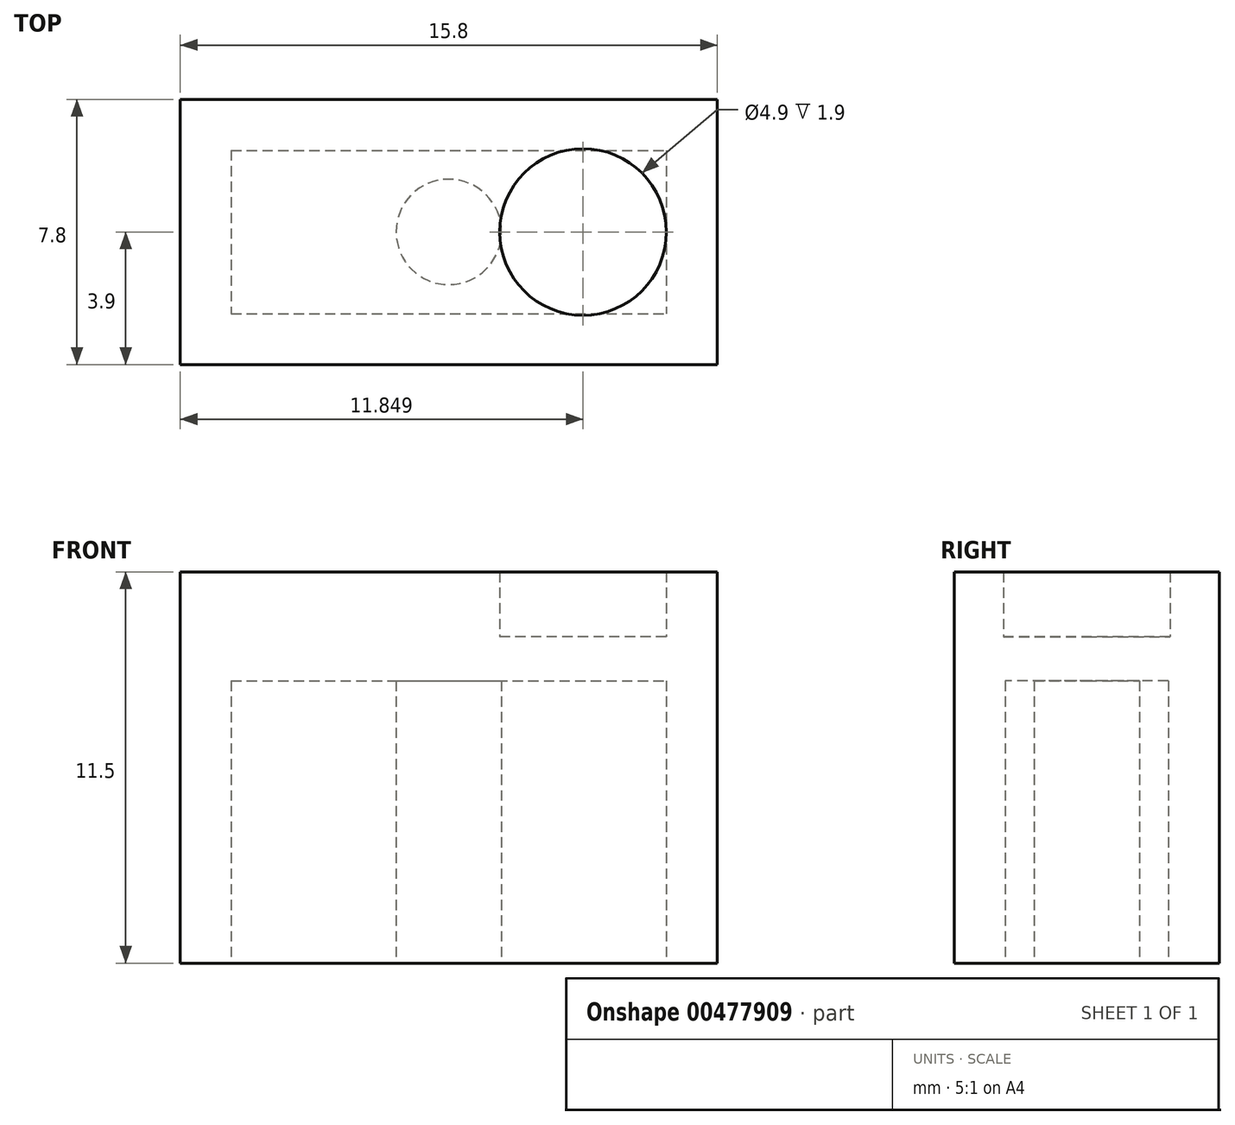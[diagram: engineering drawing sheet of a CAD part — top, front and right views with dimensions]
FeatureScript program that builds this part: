
annotation { "Feature Type Name" : "Feature", "Feature Type Description" : "" }
export const myFeature = defineFeature(function(context is Context, id is Id, definition is map)
    precondition{}
    {
        {
            var Q0;
            Q0=qCreatedBy(makeId("Front.planeOp"),FACE);
            var sketch = newSketch(context, id + "F0", { "sketchPlane" : qUnion([Q0])});
            skLineSegment(sketch, "E0", {"start": v(-64.18, -22.45) * mm, "end": v(-48.38, -22.45) * mm});
            skLineSegment(sketch, "E1", {"start": v(-48.38, -22.45) * mm, "end": v(-48.38, -12.85) * mm});
            skLineSegment(sketch, "E2", {"start": v(-48.38, -12.85) * mm, "end": v(-64.18, -12.85) * mm});
            skLineSegment(sketch, "E3", {"start": v(-64.18, -12.85) * mm, "end": v(-64.18, -22.45) * mm});
            skSolve(sketch);
        }
        {
            var Q0;
            Q0=makeQuery(id+"F0.imprint","IMPRINT",FACE,{"disambiguationData":[TD([[makeQuery(id+"F0.imprint","IMPRINT",EDGE,{"derivedFrom":sQuery(id+"F0.wireOp",EDGE,"E0")}),1.0]])]});
            extrude(context, id + "F1", {"entities" : qUnion([Q0]), "depth" : 7.8 * mm});
        }
        {
            var Q0;
            Q0=makeQuery(id+"F1.opExtrude","SWEPT_FACE",FACE,{"disambiguationData":[OSD([sQuery(id+"F0.wireOp",EDGE,"E2")])]});
            var sketch = newSketch(context, id + "F2", { "sketchPlane" : qUnion([Q0])});
            skLineSegment(sketch, "E4", {"start": v(-56.28, 0) * mm, "end": v(-56.28, -7.8) * mm, "construction": true});
            skCircle(sketch, "E5", {"center": v(-60.23, -3.9) * mm, "radius": 2.45 * mm});
            skCircle(sketch, "E6.MirrorC", {"center": v(-52.33, -3.9) * mm, "radius": 2.45 * mm});
            skSolve(sketch);
        }
        {
            var Q0;
            Q0=makeQuery(id+"F2.imprint","IMPRINT",FACE,{"disambiguationData":[TD([[makeQuery(id+"F2.imprint","IMPRINT",EDGE,{"derivedFrom":sQuery(id+"F2.wireOp",EDGE,"E5")}),1.0]])]});
            var Q1;
            Q1=makeQuery(id+"F2.imprint","IMPRINT",FACE,{"disambiguationData":[TD([[makeQuery(id+"F2.imprint","IMPRINT",EDGE,{"derivedFrom":sQuery(id+"F2.wireOp",EDGE,"E6.MirrorC")}),-1.0]])]});
            var Q2;
            Q2=sQuery(id+"F2.wireOp",EDGE,"E6.MirrorC");
            var Q3;
            Q3=sQuery(id+"F2.wireOp",EDGE,"E5");
            extrude(context, id + "F3", {"entities" : qUnion([Q0, Q1]), "operationType" : NewBodyOperationType.ADD, "surfaceEntities" : qUnion([Q2, Q3]), "depth" : 1.9 * mm});
        }
        {
            var Q0;
            Q0=makeQuery(id+"F1.opExtrude","SWEPT_FACE",FACE,{"disambiguationData":[OSD([sQuery(id+"F0.wireOp",EDGE,"E0")])]});
            var sketch = newSketch(context, id + "F4", { "sketchPlane" : qUnion([Q0])});
            skPoint(sketch, "E7.endSnap0", {"position": v(-56.28, 7.8) * mm});
            skLineSegment(sketch, "E8", {"start": v(-56.28, 1.5) * mm, "end": v(-62.68, 1.5) * mm, "construction": true});
            skLineSegment(sketch, "E9.bottom", {"start": v(-62.68, 1.5) * mm, "end": v(-49.88, 1.5) * mm});
            skLineSegment(sketch, "E9.top", {"start": v(-62.68, 6.3) * mm, "end": v(-49.88, 6.3) * mm});
            skLineSegment(sketch, "E9.left", {"start": v(-62.68, 1.5) * mm, "end": v(-62.68, 6.3) * mm});
            skLineSegment(sketch, "E9.right", {"start": v(-49.88, 1.5) * mm, "end": v(-49.88, 6.3) * mm});
            skLineSegment(sketch, "E10", {"start": v(-62.68, 6.3) * mm, "end": v(-49.88, 1.5) * mm, "construction": true});
            skCircle(sketch, "E11", {"center": v(-56.28, 3.9) * mm, "radius": 1.55 * mm});
            skSolve(sketch);
        }
        {
            var Q0;
            Q0=makeQuery(id+"F4.imprint","IMPRINT",FACE,{"disambiguationData":[TD([[makeQuery(id+"F4.imprint","IMPRINT",EDGE,{"derivedFrom":sQuery(id+"F4.wireOp",EDGE,"E9.bottom")}),1.0]])]});
            extrude(context, id + "F5", {"entities" : qUnion([Q0]), "operationType" : NewBodyOperationType.REMOVE, "oppositeDirection" : true, "depth" : 8.3 * mm});
        }
    });
